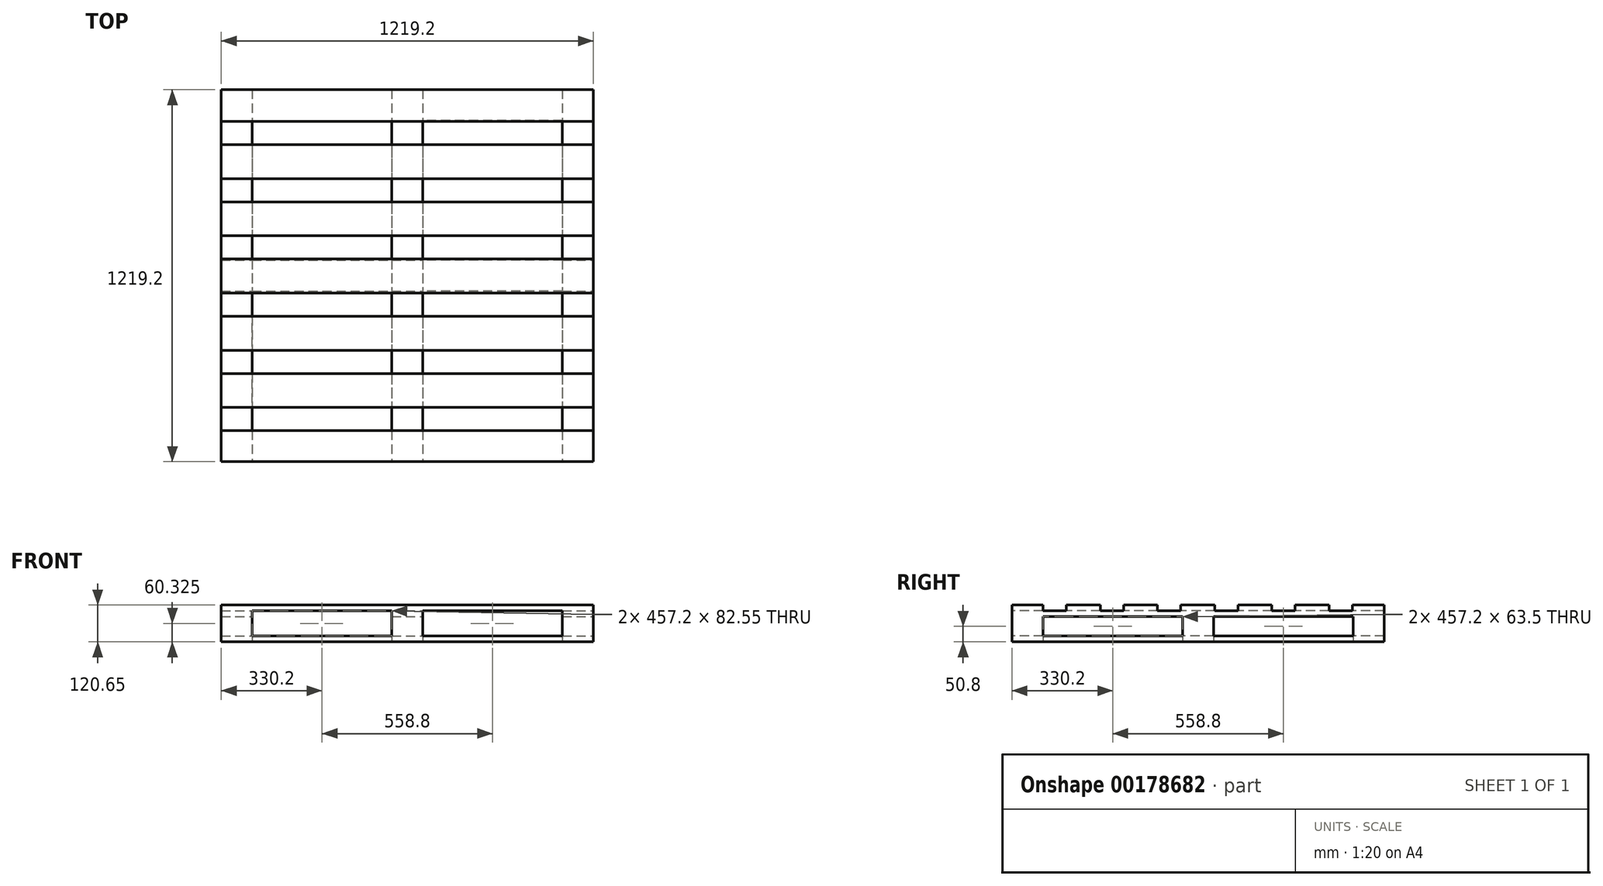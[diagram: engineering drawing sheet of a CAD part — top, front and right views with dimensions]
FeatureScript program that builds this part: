
annotation { "Feature Type Name" : "Feature", "Feature Type Description" : "" }
export const myFeature = defineFeature(function(context is Context, id is Id, definition is map)
    precondition{}
    {
        {
            var Q0;
            Q0=qCreatedBy(makeId("Front.planeOp"),FACE);
            var sketch = newSketch(context, id + "F0", { "sketchPlane" : qUnion([Q0])});
            skLineSegment(sketch, "E0.bottom", {"start": v(609.6, 50.8) * mm, "end": v(-609.6, 50.8) * mm});
            skLineSegment(sketch, "E0.top", {"start": v(609.6, -50.8) * mm, "end": v(-609.6, -50.8) * mm});
            skLineSegment(sketch, "E0.left", {"start": v(609.6, 50.8) * mm, "end": v(609.6, -50.8) * mm});
            skLineSegment(sketch, "E0.right", {"start": v(-609.6, 50.8) * mm, "end": v(-609.6, -50.8) * mm});
            skPoint(sketch, "E0.middle", {"position": v(0, 0) * mm});
            skSolve(sketch);
        }
        {
            var Q0;
            Q0=makeQuery(id+"F0.imprint","IMPRINT",FACE,{"disambiguationData":[TD([[makeQuery(id+"F0.imprint","IMPRINT",EDGE,{"derivedFrom":sQuery(id+"F0.wireOp",EDGE,"E0.bottom")}),1.0]])]});
            extrude(context, id + "F1", {"entities" : qUnion([Q0]), "endBound" : BoundingType.SYMMETRIC, "depth" : 1219.2 * mm});
        }
        {
            var Q0;
            Q0=makeQuery(id+"F1.opExtrude","CAP_FACE",FACE,{"disambiguationData":[OSD([sQuery(id+"F0.wireOp",EDGE,"E0.bottom"),sQuery(id+"F0.wireOp",EDGE,"E0.top"),sQuery(id+"F0.wireOp",EDGE,"E0.left"),sQuery(id+"F0.wireOp",EDGE,"E0.right")])],"isStart":false});
            var sketch = newSketch(context, id + "F2", { "sketchPlane" : qUnion([Q0])});
            skLineSegment(sketch, "E1.bottom", {"start": v(-50.8, 31.75) * mm, "end": v(-508, 31.75) * mm});
            skLineSegment(sketch, "E1.top", {"start": v(-50.8, -31.75) * mm, "end": v(-508, -31.75) * mm});
            skLineSegment(sketch, "E1.left", {"start": v(-50.8, 31.75) * mm, "end": v(-50.8, -31.75) * mm});
            skLineSegment(sketch, "E1.right", {"start": v(-508, 31.75) * mm, "end": v(-508, -31.75) * mm});
            skPoint(sketch, "E1.middle", {"position": v(-279.4, 0) * mm});
            skLineSegment(sketch, "E2", {"start": v(0, 50.8) * mm, "end": v(0, -50.8) * mm, "construction": true});
            skPoint(sketch, "E3.MirrorP", {"position": v(279.4, 0) * mm});
            skLineSegment(sketch, "E4.MirrorCS", {"start": v(50.8, 31.75) * mm, "end": v(508, 31.75) * mm});
            skLineSegment(sketch, "E5.MirrorCS", {"start": v(50.8, -31.75) * mm, "end": v(508, -31.75) * mm});
            skLineSegment(sketch, "E6.MirrorCS", {"start": v(50.8, 31.75) * mm, "end": v(50.8, -31.75) * mm});
            skLineSegment(sketch, "E7.MirrorCS", {"start": v(508, 31.75) * mm, "end": v(508, -31.75) * mm});
            skSolve(sketch);
        }
        {
            var Q0;
            Q0 = qSketchRegion(id + "F2", true);
            extrude(context, id + "F3", {"entities" : qUnion([Q0]), "operationType" : NewBodyOperationType.REMOVE, "endBound" : BoundingType.THROUGH_ALL, "oppositeDirection" : true, "depth" : 25.4 * mm});
        }
        {
            var Q0;
            Q0=makeQuery(id+"F1.opExtrude","SWEPT_FACE",FACE,{"disambiguationData":[OSD([sQuery(id+"F0.wireOp",EDGE,"E0.left")])]});
            var sketch = newSketch(context, id + "F4", { "sketchPlane" : qUnion([Q0])});
            skLineSegment(sketch, "E8.bottom", {"start": v(-508, 31.75) * mm, "end": v(-50.8, 31.75) * mm});
            skLineSegment(sketch, "E8.top", {"start": v(-508, -31.75) * mm, "end": v(-50.8, -31.75) * mm});
            skLineSegment(sketch, "E8.left", {"start": v(-508, 31.75) * mm, "end": v(-508, -31.75) * mm});
            skLineSegment(sketch, "E8.right", {"start": v(-50.8, 31.75) * mm, "end": v(-50.8, -31.75) * mm});
            skPoint(sketch, "E8.middle", {"position": v(-279.4, 0) * mm});
            skLineSegment(sketch, "E9", {"start": v(0, 50.8) * mm, "end": v(0, -50.8) * mm, "construction": true});
            skLineSegment(sketch, "E10.MirrorCS", {"start": v(508, 31.75) * mm, "end": v(50.8, 31.75) * mm});
            skPoint(sketch, "E11.MirrorP", {"position": v(279.4, 0) * mm});
            skLineSegment(sketch, "E12.MirrorCS", {"start": v(508, -31.75) * mm, "end": v(50.8, -31.75) * mm});
            skLineSegment(sketch, "E13.MirrorCS", {"start": v(508, 31.75) * mm, "end": v(508, -31.75) * mm});
            skLineSegment(sketch, "E14.MirrorCS", {"start": v(50.8, 31.75) * mm, "end": v(50.8, -31.75) * mm});
            skSolve(sketch);
        }
        {
            var Q0;
            Q0 = qSketchRegion(id + "F4", true);
            extrude(context, id + "F5", {"entities" : qUnion([Q0]), "operationType" : NewBodyOperationType.REMOVE, "endBound" : BoundingType.THROUGH_ALL, "oppositeDirection" : true, "depth" : 25.4 * mm});
        }
        {
            var Q0;
            Q0=makeQuery(id+"F1.opExtrude","SWEPT_FACE",FACE,{"disambiguationData":[OSD([sQuery(id+"F0.wireOp",EDGE,"E0.top")])]});
            var sketch = newSketch(context, id + "F6", { "sketchPlane" : qUnion([Q0])});
            skLineSegment(sketch, "E15", {"start": v(0, 0) * mm, "end": v(0, 609.6) * mm, "construction": true});
            skLineSegment(sketch, "E16", {"start": v(0, 0) * mm, "end": v(0, -609.6) * mm, "construction": true});
            skLineSegment(sketch, "E17", {"start": v(-609.6, 0) * mm, "end": v(609.6, 0) * mm, "construction": true});
            skLineSegment(sketch, "E18.bottom", {"start": v(508, 508) * mm, "end": v(50.8, 508) * mm});
            skLineSegment(sketch, "E18.top", {"start": v(508, 50.8) * mm, "end": v(50.8, 50.8) * mm});
            skLineSegment(sketch, "E18.left", {"start": v(508, 508) * mm, "end": v(508, 50.8) * mm});
            skLineSegment(sketch, "E18.right", {"start": v(50.8, 508) * mm, "end": v(50.8, 50.8) * mm});
            skPoint(sketch, "E18.middle", {"position": v(279.4, 279.4) * mm});
            skLineSegment(sketch, "E19.MirrorCS", {"start": v(-508, 50.8) * mm, "end": v(-50.8, 50.8) * mm});
            skLineSegment(sketch, "E20.MirrorCS", {"start": v(-50.8, 508) * mm, "end": v(-50.8, 50.8) * mm});
            skLineSegment(sketch, "E21.MirrorCS", {"start": v(-508, 508) * mm, "end": v(-50.8, 508) * mm});
            skLineSegment(sketch, "E22.MirrorCS", {"start": v(-508, 508) * mm, "end": v(-508, 50.8) * mm});
            skLineSegment(sketch, "E23.MirrorCS", {"start": v(508, -508) * mm, "end": v(50.8, -508) * mm});
            skLineSegment(sketch, "E24.MirrorCS", {"start": v(508, -50.8) * mm, "end": v(50.8, -50.8) * mm});
            skLineSegment(sketch, "E25.MirrorCS", {"start": v(508, -508) * mm, "end": v(508, -50.8) * mm});
            skPoint(sketch, "E26.MirrorP", {"position": v(279.4, -279.4) * mm});
            skLineSegment(sketch, "E27.MirrorCS", {"start": v(50.8, -508) * mm, "end": v(50.8, -50.8) * mm});
            skLineSegment(sketch, "E28.MirrorCS", {"start": v(-508, -50.8) * mm, "end": v(-50.8, -50.8) * mm});
            skLineSegment(sketch, "E29.MirrorCS", {"start": v(-50.8, -508) * mm, "end": v(-50.8, -50.8) * mm});
            skLineSegment(sketch, "E30.MirrorCS", {"start": v(-508, -508) * mm, "end": v(-50.8, -508) * mm});
            skLineSegment(sketch, "E31.MirrorCS", {"start": v(-508, -508) * mm, "end": v(-508, -50.8) * mm});
            skSolve(sketch);
        }
        {
            var Q0;
            Q0 = qSketchRegion(id + "F6", true);
            extrude(context, id + "F7", {"entities" : qUnion([Q0]), "operationType" : NewBodyOperationType.REMOVE, "oppositeDirection" : true, "depth" : 25.4 * mm});
        }
        {
            var Q0;
            Q0=makeQuery(id+"F1.opExtrude","CAP_FACE",FACE,{"disambiguationData":[OSD([sQuery(id+"F0.wireOp",EDGE,"E0.bottom"),sQuery(id+"F0.wireOp",EDGE,"E0.top"),sQuery(id+"F0.wireOp",EDGE,"E0.left"),sQuery(id+"F0.wireOp",EDGE,"E0.right")])],"isStart":false});
            var sketch = newSketch(context, id + "F8", { "sketchPlane" : qUnion([Q0])});
            skLineSegment(sketch, "E32.bottom", {"start": v(-508, 50.8) * mm, "end": v(-50.8, 50.8) * mm});
            skLineSegment(sketch, "E32.top", {"start": v(-508, 31.75) * mm, "end": v(-50.8, 31.75) * mm});
            skLineSegment(sketch, "E32.left", {"start": v(-508, 50.8) * mm, "end": v(-508, 31.75) * mm});
            skLineSegment(sketch, "E32.right", {"start": v(-50.8, 50.8) * mm, "end": v(-50.8, 31.75) * mm});
            skLineSegment(sketch, "E33.MirrorCS", {"start": v(508, 50.8) * mm, "end": v(508, 31.75) * mm});
            skLineSegment(sketch, "E34.MirrorCS", {"start": v(50.8, 50.8) * mm, "end": v(50.8, 31.75) * mm});
            skLineSegment(sketch, "E35.MirrorCS", {"start": v(508, 31.75) * mm, "end": v(50.8, 31.75) * mm});
            skLineSegment(sketch, "E36.MirrorCS", {"start": v(508, 50.8) * mm, "end": v(50.8, 50.8) * mm});
            skSolve(sketch);
        }
        {
            var Q0;
            Q0 = qSketchRegion(id + "F8", true);
            extrude(context, id + "F9", {"entities" : qUnion([Q0]), "operationType" : NewBodyOperationType.REMOVE, "endBound" : BoundingType.THROUGH_ALL, "oppositeDirection" : true, "depth" : 25.4 * mm});
        }
        {
            var Q0;
            {var subQ0=sQuery(id+"F0.wireOp",EDGE,"E0.left");var subQ3=sQuery(id+"F0.wireOp",EDGE,"E0.bottom");Q0=makeQuery(id+"F9.boolean.opBoolean","SPLIT",FACE,{"disambiguationData":[TD([makeQuery(id+"F1.opExtrude","SWEPT_FACE",FACE,{"disambiguationData":[OSD([subQ0])]})])],"derivedFrom":makeQuery(id+"F1.opExtrude","SWEPT_FACE",FACE,{"disambiguationData":[OSD([subQ3])]})});}
            var sketch = newSketch(context, id + "F10", { "sketchPlane" : qUnion([Q0])});
            skLineSegment(sketch, "E37.bottom", {"start": v(609.6, -609.6) * mm, "end": v(-609.6, -609.6) * mm});
            skLineSegment(sketch, "E37.top", {"start": v(609.6, 609.6) * mm, "end": v(-609.6, 609.6) * mm});
            skLineSegment(sketch, "E37.left", {"start": v(609.6, -609.6) * mm, "end": v(609.6, 609.6) * mm});
            skLineSegment(sketch, "E37.right", {"start": v(-609.6, -609.6) * mm, "end": v(-609.6, 609.6) * mm});
            skSolve(sketch);
        }
        {
            var Q0;
            Q0 = qSketchRegion(id + "F10", true);
            extrude(context, id + "F11", {"entities" : qUnion([Q0]), "operationType" : NewBodyOperationType.ADD, "depth" : 19.05 * mm});
        }
        {
            var Q0;
            Q0=makeQuery(id+"F11.boolean.opBoolean","MERGE",FACE,{"derivedFrom":[makeQuery(id+"F1.opExtrude","SWEPT_FACE",FACE,{"disambiguationData":[OSD([sQuery(id+"F0.wireOp",EDGE,"E0.left")])]}),makeQuery(id+"F11.opExtrude","SWEPT_FACE",FACE,{"disambiguationData":[OSD([sQuery(id+"F10.wireOp",EDGE,"E37.left")])]})]});
            var sketch = newSketch(context, id + "F12", { "sketchPlane" : qUnion([Q0])});
            skLineSegment(sketch, "E38.bottom", {"start": v(-508, 69.85) * mm, "end": v(-431.8, 69.85) * mm});
            skLineSegment(sketch, "E38.top", {"start": v(-508, 50.8) * mm, "end": v(-431.8, 50.8) * mm});
            skLineSegment(sketch, "E38.left", {"start": v(-508, 69.85) * mm, "end": v(-508, 50.8) * mm});
            skLineSegment(sketch, "E38.right", {"start": v(-431.8, 69.85) * mm, "end": v(-431.8, 50.8) * mm});
            skLineSegment(sketch, "E39.1.0.0", {"start": v(-244.35, 69.85) * mm, "end": v(-244.35, 50.8) * mm});
            skLineSegment(sketch, "E39.1.0.1", {"start": v(-320.55, 69.85) * mm, "end": v(-320.55, 50.8) * mm});
            skLineSegment(sketch, "E39.1.0.2", {"start": v(-320.55, 50.8) * mm, "end": v(-244.35, 50.8) * mm});
            skLineSegment(sketch, "E39.1.0.3", {"start": v(-320.55, 69.85) * mm, "end": v(-244.35, 69.85) * mm});
            skLineSegment(sketch, "E39.2.0.0", {"start": v(-56.9, 69.85) * mm, "end": v(-56.9, 50.8) * mm});
            skLineSegment(sketch, "E39.2.0.1", {"start": v(-133.1, 69.85) * mm, "end": v(-133.1, 50.8) * mm});
            skLineSegment(sketch, "E39.2.0.2", {"start": v(-133.1, 50.8) * mm, "end": v(-56.9, 50.8) * mm});
            skLineSegment(sketch, "E39.2.0.3", {"start": v(-133.1, 69.85) * mm, "end": v(-56.9, 69.85) * mm});
            skLineSegment(sketch, "E39.3.0.0", {"start": v(130.56, 69.85) * mm, "end": v(130.56, 50.8) * mm});
            skLineSegment(sketch, "E39.3.0.1", {"start": v(54.36, 69.85) * mm, "end": v(54.36, 50.8) * mm});
            skLineSegment(sketch, "E39.3.0.2", {"start": v(54.36, 50.8) * mm, "end": v(130.56, 50.8) * mm});
            skLineSegment(sketch, "E39.3.0.3", {"start": v(54.36, 69.85) * mm, "end": v(130.56, 69.85) * mm});
            skLineSegment(sketch, "E39.4.0.0", {"start": v(318, 69.85) * mm, "end": v(318, 50.8) * mm});
            skLineSegment(sketch, "E39.4.0.1", {"start": v(241.8, 69.85) * mm, "end": v(241.8, 50.8) * mm});
            skLineSegment(sketch, "E39.4.0.2", {"start": v(241.8, 50.8) * mm, "end": v(318, 50.8) * mm});
            skLineSegment(sketch, "E39.4.0.3", {"start": v(241.8, 69.85) * mm, "end": v(318, 69.85) * mm});
            skLineSegment(sketch, "E39.5.0.0", {"start": v(505.46, 69.85) * mm, "end": v(505.46, 50.8) * mm});
            skLineSegment(sketch, "E39.5.0.1", {"start": v(429.26, 69.85) * mm, "end": v(429.26, 50.8) * mm});
            skLineSegment(sketch, "E39.5.0.2", {"start": v(429.26, 50.8) * mm, "end": v(505.46, 50.8) * mm});
            skLineSegment(sketch, "E39.5.0.3", {"start": v(429.26, 69.85) * mm, "end": v(505.46, 69.85) * mm});
            skLineSegment(sketch, "E39.direction1", {"start": v(-508, 50.8) * mm, "end": v(-320.55, 50.8) * mm, "construction": true});
            skSolve(sketch);
        }
        {
            var Q0;
            Q0 = qSketchRegion(id + "F12", true);
            extrude(context, id + "F13", {"entities" : qUnion([Q0]), "operationType" : NewBodyOperationType.REMOVE, "endBound" : BoundingType.THROUGH_ALL, "oppositeDirection" : true, "depth" : 25.4 * mm});
        }
    });
